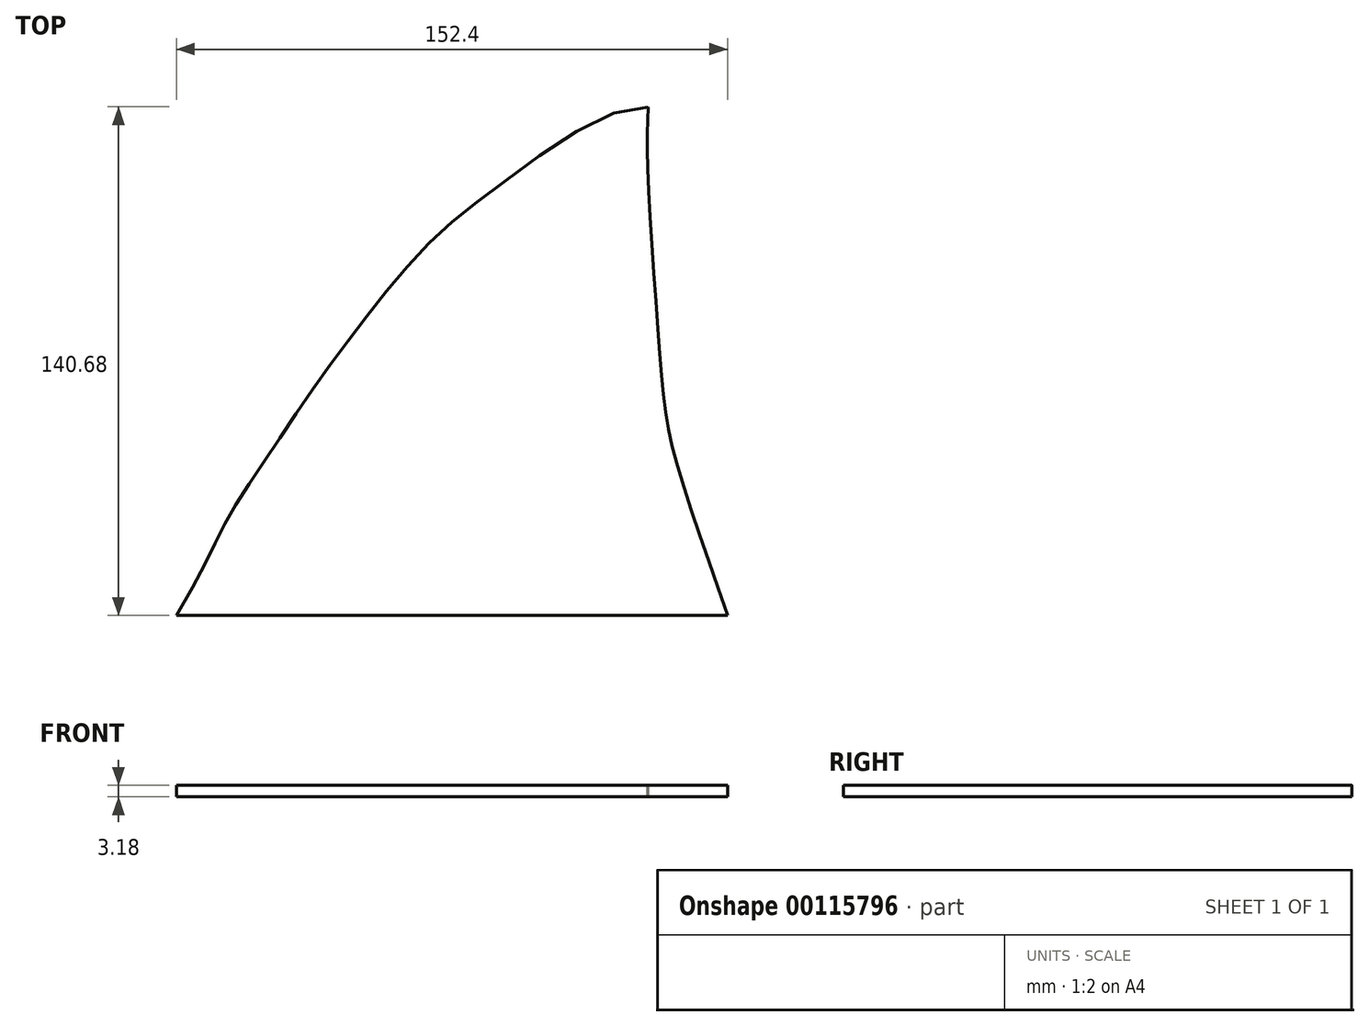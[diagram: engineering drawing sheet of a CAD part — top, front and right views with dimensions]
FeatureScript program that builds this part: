
annotation { "Feature Type Name" : "Feature", "Feature Type Description" : "" }
export const myFeature = defineFeature(function(context is Context, id is Id, definition is map)
    precondition{}
    {
        {
            var Q0;
            Q0=qCreatedBy(makeId("Top.planeOp"),FACE);
            var sketch = newSketch(context, id + "F0", { "sketchPlane" : qUnion([Q0])});
            skFitSpline(sketch, "E0", {"points": [v(-96.01, -74.31) * mm, v(-86.2, -56.15) * mm, v(-80.34, -44.9) * mm, v(-70.9, -30.5) * mm, v(-58.18, -11.5) * mm, v(-44.02, 7.6) * mm, v(-26.22, 28.64) * mm, v(-3.56, 47.08) * mm, v(34.4, 66.35) * mm], "startDerivative": vector(119.9, 196.35) * mm, "endDerivative": vector(203.96, -10.63) * mm});
            skFitSpline(sketch, "E1", {"points": [v(34.4, 66.35) * mm, v(34.4, 48.32) * mm, v(37.8, -3.41) * mm, v(41.37, -28.54) * mm, v(56.39, -74.31) * mm], "startDerivative": vector(-3.12, -80.48) * mm, "endDerivative": vector(60.11, -177.32) * mm});
            skLineSegment(sketch, "E2", {"start": v(-96.01, -74.31) * mm, "end": v(56.39, -74.31) * mm});
            skSolve(sketch);
        }
        {
            var Q0;
            Q0=makeQuery(id+"F0.imprint","IMPRINT",FACE,{"disambiguationData":[TD([[makeQuery(id+"F0.imprint","IMPRINT",EDGE,{"derivedFrom":sQuery(id+"F0.wireOp",EDGE,"E0")}),-1.0]])]});
            extrude(context, id + "F1", {"entities" : qUnion([Q0]), "depth" : 3.17 * mm});
        }
    });
